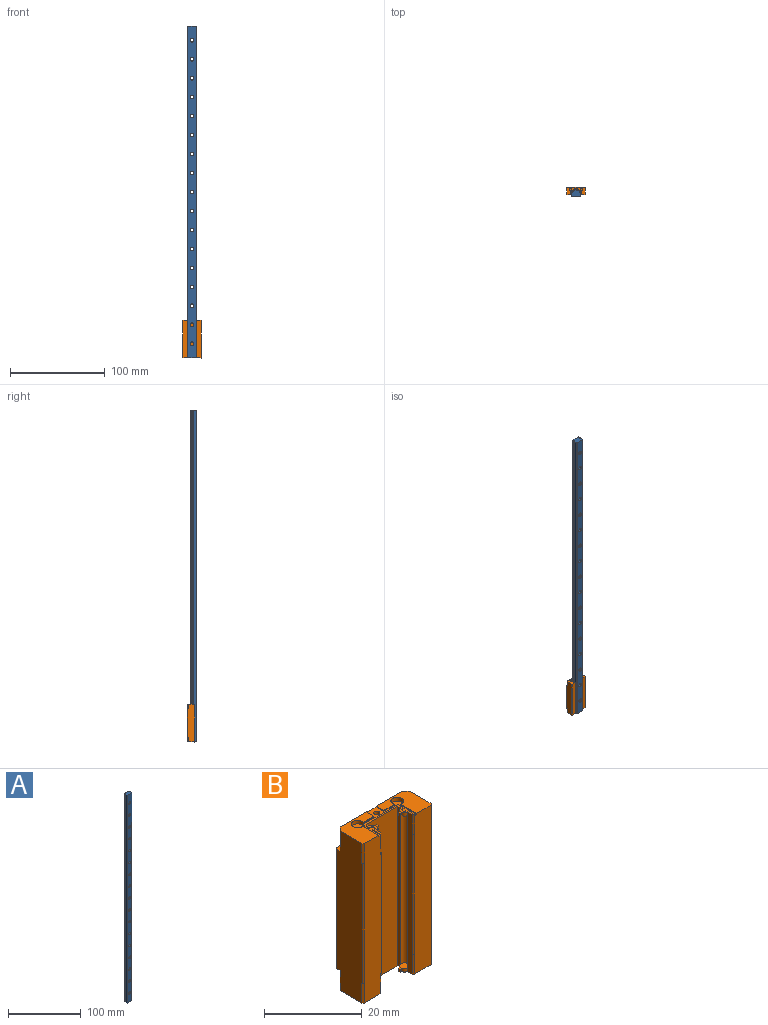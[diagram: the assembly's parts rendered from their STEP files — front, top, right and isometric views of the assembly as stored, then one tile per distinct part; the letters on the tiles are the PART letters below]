
ASSEMBLY  parts=2 mates=1
PART A: 107 faces, bbox 9x6.5x350 mm
  f0: cylinder r=1.75mm len=3.5mm, axis (0,1,0), area 30.8mm2, adj f36,f43
  f1: cylinder r=1.75mm len=3.5mm, axis (0,1,0), area 30.8mm2, adj f34,f41
  f2: cylinder r=1.75mm len=3.5mm, axis (0,1,0), area 30.8mm2, adj f32,f39
  f3: cylinder r=1.75mm len=3.5mm, axis (0,1,0), area 30.8mm2, adj f30,f37
  f4: cylinder r=1.75mm len=3.5mm, axis (0,1,0), area 30.8mm2, adj f26,f27
  f5: cylinder r=1mm len=350mm, axis (0,0,-1), area 403.5mm2, adj f6,f24,f57,f106
  f6: plane 350x0.5mm, normal (0,-1,0), area 175mm2, adj f5,f7,f57,f106
  f7: plane 350x0.5mm, normal (-1,0,0), area 175mm2, adj f6,f8,f57,f106
  f8: plane 350x0.47mm, normal (0,1,0), area 163.7mm2, adj f7,f9,f57,f106
  f9: cylinder r=1mm len=350mm, axis (0,0,-1), area 448.7mm2, adj f8,f10,f57,f106
  f10: plane 350x3.51mm, normal (-1,0,0), area 1226.8mm2, adj f9,f11,f57,f106
  f11: plane 350x0.2mm, normal (-0.71,-0.71,0), area 99mm2, adj f10,f12,f57,f106
  f12: plane 350x8.6mm, normal (0,-1,0), area 2806.9mm2, adj f11,f13,f27,f37,f39,f41,f43,f57
  f13: plane 350x0.2mm, normal (0.71,-0.71,0), area 99mm2, adj f12,f14,f57,f106
  f14: plane 350x3.51mm, normal (1,0,0), area 1226.8mm2, adj f13,f15,f57,f106
  f15: cylinder r=1mm len=350mm, axis (0,0,-1), area 448.7mm2, adj f14,f16,f57,f106
  f16: plane 350x0.47mm, normal (0,1,0), area 163.7mm2, adj f15,f17,f57,f106
  f17: plane 350x0.5mm, normal (1,0,0), area 175mm2, adj f16,f18,f57,f106
  f18: plane 350x0.5mm, normal (0,-1,0), area 175mm2, adj f17,f19,f57,f106
  f19: cylinder r=1mm len=350mm, axis (0,0,-1), area 403.5mm2, adj f18,f20,f57,f106
  f20: plane 350x0.61mm, normal (1,0,0), area 211.8mm2, adj f19,f21,f57,f106
  f21: plane 350x0.2mm, normal (0.71,0.71,0), area 99mm2, adj f20,f22,f57,f106
  f22: plane 350x8.6mm, normal (0,1,0), area 2463.1mm2, adj f21,f23,f28,f38,f40,f42,f44,f57
  f23: plane 350x0.2mm, normal (-0.71,0.71,0), area 99mm2, adj f22,f24,f57,f106
  f24: plane 350x0.61mm, normal (-1,0,0), area 211.8mm2, adj f5,f23,f57,f106
  f25: cylinder r=3mm len=6mm, axis (0,1,0), area 62.2mm2, adj f26,f28
  f26: plane 6x6mm, normal (0,1,0), area 18.7mm2, adj f4,f25
  f27: cone r=1.75mm half-angle=45deg, axis (0,-1,0), area 3.3mm2, adj f4,f12
  f28: cone r=3mm half-angle=45deg, axis (0,1,0), area 5.5mm2, adj f22,f25
  f29: cylinder r=3mm len=6mm, axis (0,1,0), area 62.2mm2, adj f30,f38
  f30: plane 6x6mm, normal (0,1,0), area 18.7mm2, adj f3,f29
  f31: cylinder r=3mm len=6mm, axis (0,1,0), area 62.2mm2, adj f32,f40
  f32: plane 6x6mm, normal (0,1,0), area 18.7mm2, adj f2,f31
  f33: cylinder r=3mm len=6mm, axis (0,1,0), area 62.2mm2, adj f34,f42
  f34: plane 6x6mm, normal (0,1,0), area 18.7mm2, adj f1,f33
  f35: cylinder r=3mm len=6mm, axis (0,1,0), area 62.2mm2, adj f36,f44
  f36: plane 6x6mm, normal (0,1,0), area 18.7mm2, adj f0,f35
  f37: cone r=1.75mm half-angle=45deg, axis (0,-1,0), area 3.3mm2, adj f3,f12
  f38: cone r=3mm half-angle=45deg, axis (0,1,0), area 5.5mm2, adj f22,f29
  f39: cone r=1.75mm half-angle=45deg, axis (0,-1,0), area 3.3mm2, adj f2,f12
  f40: cone r=3mm half-angle=45deg, axis (0,1,0), area 5.5mm2, adj f22,f31
  f41: cone r=1.75mm half-angle=45deg, axis (0,-1,0), area 3.3mm2, adj f1,f12
  f42: cone r=3mm half-angle=45deg, axis (0,1,0), area 5.5mm2, adj f22,f33
  f43: cone r=1.75mm half-angle=45deg, axis (0,-1,0), area 3.3mm2, adj f0,f12
  f44: cone r=3mm half-angle=45deg, axis (0,1,0), area 5.5mm2, adj f22,f35
  f45: cylinder r=1.75mm len=3.5mm, axis (0,1,0), area 30.8mm2, adj f83,f104
  f46: cylinder r=1.75mm len=3.5mm, axis (0,1,0), area 30.8mm2, adj f81,f102
  f47: cylinder r=1.75mm len=3.5mm, axis (0,1,0), area 30.8mm2, adj f79,f100
  f48: cylinder r=1.75mm len=3.5mm, axis (0,1,0), area 30.8mm2, adj f77,f98
  f49: cylinder r=1.75mm len=3.5mm, axis (0,1,0), area 30.8mm2, adj f75,f96
  f50: cylinder r=1.75mm len=3.5mm, axis (0,1,0), area 30.8mm2, adj f73,f94
  f51: cylinder r=1.75mm len=3.5mm, axis (0,1,0), area 30.8mm2, adj f71,f92
  f52: cylinder r=1.75mm len=3.5mm, axis (0,1,0), area 30.8mm2, adj f69,f90
  f53: cylinder r=1.75mm len=3.5mm, axis (0,1,0), area 30.8mm2, adj f67,f88
  f54: cylinder r=1.75mm len=3.5mm, axis (0,1,0), area 30.8mm2, adj f65,f86
  f55: cylinder r=1.75mm len=3.5mm, axis (0,1,0), area 30.8mm2, adj f63,f84
  f56: cylinder r=1.75mm len=3.5mm, axis (0,1,0), area 30.8mm2, adj f59,f60
  f57: plane 9x6.5mm, normal (0,0,-1), area 55.2mm2, adj f5,f6,f7,f8,f9,f10,f11,f12
  f58: cylinder r=3mm len=6mm, axis (0,1,0), area 62.2mm2, adj f59,f61
  f59: plane 6x6mm, normal (0,1,0), area 18.7mm2, adj f56,f58
  f60: cone r=1.75mm half-angle=45deg, axis (0,-1,0), area 3.3mm2, adj f12,f56
  f61: cone r=3mm half-angle=45deg, axis (0,1,0), area 5.5mm2, adj f22,f58
  f62: cylinder r=3mm len=6mm, axis (0,1,0), area 62.2mm2, adj f63,f85
  f63: plane 6x6mm, normal (0,1,0), area 18.7mm2, adj f55,f62
  f64: cylinder r=3mm len=6mm, axis (0,1,0), area 62.2mm2, adj f65,f87
  f65: plane 6x6mm, normal (0,1,0), area 18.7mm2, adj f54,f64
  f66: cylinder r=3mm len=6mm, axis (0,1,0), area 62.2mm2, adj f67,f89
  f67: plane 6x6mm, normal (0,1,0), area 18.7mm2, adj f53,f66
  f68: cylinder r=3mm len=6mm, axis (0,1,0), area 62.2mm2, adj f69,f91
  f69: plane 6x6mm, normal (0,1,0), area 18.7mm2, adj f52,f68
  f70: cylinder r=3mm len=6mm, axis (0,1,0), area 62.2mm2, adj f71,f93
  f71: plane 6x6mm, normal (0,1,0), area 18.7mm2, adj f51,f70
  f72: cylinder r=3mm len=6mm, axis (0,1,0), area 62.2mm2, adj f73,f95
  f73: plane 6x6mm, normal (0,1,0), area 18.7mm2, adj f50,f72
  f74: cylinder r=3mm len=6mm, axis (0,1,0), area 62.2mm2, adj f75,f97
  f75: plane 6x6mm, normal (0,1,0), area 18.7mm2, adj f49,f74
  f76: cylinder r=3mm len=6mm, axis (0,1,0), area 62.2mm2, adj f77,f99
  f77: plane 6x6mm, normal (0,1,0), area 18.7mm2, adj f48,f76
  f78: cylinder r=3mm len=6mm, axis (0,1,0), area 62.2mm2, adj f79,f101
  f79: plane 6x6mm, normal (0,1,0), area 18.7mm2, adj f47,f78
  f80: cylinder r=3mm len=6mm, axis (0,1,0), area 62.2mm2, adj f81,f103
  f81: plane 6x6mm, normal (0,1,0), area 18.7mm2, adj f46,f80
  f82: cylinder r=3mm len=6mm, axis (0,1,0), area 62.2mm2, adj f83,f105
  f83: plane 6x6mm, normal (0,1,0), area 18.7mm2, adj f45,f82
  f84: cone r=1.75mm half-angle=45deg, axis (0,-1,0), area 3.3mm2, adj f12,f55
  f85: cone r=3mm half-angle=45deg, axis (0,1,0), area 5.5mm2, adj f22,f62
  f86: cone r=1.75mm half-angle=45deg, axis (0,-1,0), area 3.3mm2, adj f12,f54
  f87: cone r=3mm half-angle=45deg, axis (0,1,0), area 5.5mm2, adj f22,f64
  f88: cone r=1.75mm half-angle=45deg, axis (0,-1,0), area 3.3mm2, adj f12,f53
  f89: cone r=3mm half-angle=45deg, axis (0,1,0), area 5.5mm2, adj f22,f66
  f90: cone r=1.75mm half-angle=45deg, axis (0,-1,0), area 3.3mm2, adj f12,f52
  f91: cone r=3mm half-angle=45deg, axis (0,1,0), area 5.5mm2, adj f22,f68
  f92: cone r=1.75mm half-angle=45deg, axis (0,-1,0), area 3.3mm2, adj f12,f51
  f93: cone r=3mm half-angle=45deg, axis (0,1,0), area 5.5mm2, adj f22,f70
  f94: cone r=1.75mm half-angle=45deg, axis (0,-1,0), area 3.3mm2, adj f12,f50
  f95: cone r=3mm half-angle=45deg, axis (0,1,0), area 5.5mm2, adj f22,f72
  f96: cone r=1.75mm half-angle=45deg, axis (0,-1,0), area 3.3mm2, adj f12,f49
  f97: cone r=3mm half-angle=45deg, axis (0,1,0), area 5.5mm2, adj f22,f74
  f98: cone r=1.75mm half-angle=45deg, axis (0,-1,0), area 3.3mm2, adj f12,f48
  f99: cone r=3mm half-angle=45deg, axis (0,1,0), area 5.5mm2, adj f22,f76
  f100: cone r=1.75mm half-angle=45deg, axis (0,-1,0), area 3.3mm2, adj f12,f47
  f101: cone r=3mm half-angle=45deg, axis (0,1,0), area 5.5mm2, adj f22,f78
  f102: cone r=1.75mm half-angle=45deg, axis (0,-1,0), area 3.3mm2, adj f12,f46
  f103: cone r=3mm half-angle=45deg, axis (0,1,0), area 5.5mm2, adj f22,f80
  f104: cone r=1.75mm half-angle=45deg, axis (0,-1,0), area 3.3mm2, adj f12,f45
  f105: cone r=3mm half-angle=45deg, axis (0,1,0), area 5.5mm2, adj f22,f82
  f106: plane 9x6.5mm, normal (0,0,1), area 55.2mm2, adj f5,f6,f7,f8,f9,f10,f11,f12
PART B: 137 faces, bbox 20x8x39.9 mm
  f0: plane 0.4x0.4mm, normal (0,0,1), area 0mm2, adj f17,f18,f36,f114
  f1: plane 5.5x1.3mm, normal (0,0,1), area 2.1mm2, adj f18,f24,f25,f26,f37,f110
  f2: plane 5.5x1.3mm, normal (0,0,1), area 2.1mm2, adj f20,f23,f25,f27,f34,f109
  f3: plane 0.4x0.4mm, normal (0,0,1), area 0mm2, adj f19,f20,f35,f112
  f4: plane 0.4x0.4mm, normal (0,0,1), area 0mm2, adj f19,f28,f39,f111
  f5: plane 0.4x0.4mm, normal (0,0,1), area 0mm2, adj f17,f21,f38,f113
  f6: plane 0.4x0.4mm, normal (0,0,-1), area 0mm2, adj f17,f21,f38,f50
  f7: plane 0.4x0.4mm, normal (0,0,-1), area 0mm2, adj f19,f28,f39,f51
  f8: plane 0.4x0.4mm, normal (0,0,-1), area 0mm2, adj f19,f20,f35,f52
  f9: plane 5.5x1.3mm, normal (0,0,-1), area 2.1mm2, adj f20,f23,f25,f27,f34,f48
  f10: plane 5.5x1.3mm, normal (0,0,-1), area 2.1mm2, adj f18,f24,f25,f26,f37,f47
  f11: plane 3x3mm, normal (0,1,0), area 7.1mm2, adj f13
  f12: plane 3x3mm, normal (0,1,0), area 7.1mm2, adj f14
  f13: cylinder r=1.5mm len=3mm, axis (0,1,0), area 25.4mm2, adj f11,f15
  f14: cylinder r=1.5mm len=3mm, axis (0,1,0), area 25.4mm2, adj f12,f16
  f15: cone r=1.5mm half-angle=45deg, axis (0,1,0), area 4.4mm2, adj f13,f23
  f16: cone r=1.5mm half-angle=45deg, axis (0,1,0), area 4.4mm2, adj f14,f24
  f17: plane 39.9x4.9mm, normal (0,-1,0), area 193.3mm2, adj f0,f5,f6,f36,f38,f46,f49,f50
  f18: plane 39.9x7.4mm, normal (-1,0,0), area 284.3mm2, adj f0,f1,f10,f36,f37,f46,f47,f49
  f19: plane 39.9x4.9mm, normal (0,-1,0), area 193.3mm2, adj f3,f4,f7,f8,f35,f39,f51,f52
  f20: plane 39.9x7.4mm, normal (1,0,0), area 284.3mm2, adj f2,f3,f8,f9,f34,f35,f48,f52
  f21: plane 39.9x1.41mm, normal (1,0,0), area 55.1mm2, adj f5,f6,f31,f38,f50,f56,f64,f95
  f22: plane 39.9x0.81mm, normal (-1,0,0), area 32.1mm2, adj f29,f33,f56,f59,f95,f98
  f23: plane 29.9x4.9mm, normal (0,1,0), area 126.2mm2, adj f2,f9,f15,f27,f34,f44
  f24: plane 29.9x4.9mm, normal (0,1,0), area 126.2mm2, adj f1,f10,f16,f26,f37,f45
  f25: plane 39.9x18mm, normal (0,1,0), area 448mm2, adj f1,f2,f9,f10,f26,f27,f47,f48
  f26: plane 29.9x0.3mm, normal (0.71,0.71,0), area 12.7mm2, adj f1,f10,f24,f25
  f27: plane 29.9x0.3mm, normal (-0.71,0.71,0), area 12.7mm2, adj f2,f9,f23,f25
  f28: plane 39.9x1.41mm, normal (-1,0,0), area 55.1mm2, adj f4,f7,f29,f39,f51,f56,f63,f95
  f29: cylinder r=1mm len=38.1mm, axis (0,0,-1), area 127.3mm2, adj f22,f28,f53,f93
  f30: plane 39.9x0.81mm, normal (1,0,0), area 32.1mm2, adj f31,f33,f56,f68,f95,f107
  f31: cylinder r=1mm len=38.1mm, axis (0,0,-1), area 127.3mm2, adj f21,f30,f54,f92
  f32: cylinder r=0.64mm len=39.5mm, axis (0,0,-1), area 159.8mm2, adj f75,f120
  f33: plane 39.9x9mm, normal (0,-1,0), area 359.1mm2, adj f22,f30,f56,f95
  f34: plane 29.9x0.3mm, normal (0.71,0.71,0), area 12.7mm2, adj f2,f9,f20,f23
  f35: plane 29.9x0.3mm, normal (0.71,-0.71,0), area 12.7mm2, adj f3,f8,f19,f20
  f36: plane 29.9x0.3mm, normal (-0.71,-0.71,0), area 12.7mm2, adj f0,f17,f18,f46
  f37: plane 29.9x0.3mm, normal (-0.71,0.71,0), area 12.7mm2, adj f1,f10,f18,f24
  f38: plane 29.9x0.3mm, normal (0.71,-0.71,0), area 12.7mm2, adj f5,f6,f17,f21
  f39: plane 29.9x0.3mm, normal (-0.71,-0.71,0), area 12.7mm2, adj f4,f7,f19,f28
  f40: plane 3x3mm, normal (0,1,0), area 7.1mm2, adj f42
  f41: plane 3x3mm, normal (0,1,0), area 7.1mm2, adj f43
  f42: cylinder r=1.5mm len=3mm, axis (0,1,0), area 25.4mm2, adj f40,f44
  f43: cylinder r=1.5mm len=3mm, axis (0,1,0), area 25.4mm2, adj f41,f45
  f44: cone r=1.5mm half-angle=45deg, axis (0,1,0), area 4.4mm2, adj f23,f42
  f45: cone r=1.5mm half-angle=45deg, axis (0,1,0), area 4.4mm2, adj f24,f43
  f46: plane 0.4x0.4mm, normal (0,0,-1), area 0mm2, adj f17,f18,f36,f49
  f47: plane 5x1mm, normal (-0.71,0.71,0), area 7.1mm2, adj f10,f18,f25,f58
  f48: plane 5x1mm, normal (0.71,0.71,0), area 7.1mm2, adj f9,f20,f25,f55
  f49: plane 5x0.4mm, normal (-0.71,-0.71,0), area 2.8mm2, adj f17,f18,f46,f58
  f50: plane 5x0.4mm, normal (0.71,-0.71,0), area 2.8mm2, adj f6,f17,f21,f56
  f51: plane 5x0.4mm, normal (-0.71,-0.71,0), area 2.8mm2, adj f7,f19,f28,f56
  f52: plane 5x0.4mm, normal (0.71,-0.71,0), area 2.8mm2, adj f8,f19,f20,f55
  f53: plane 2.47x2mm, normal (0,0,1), area 3.4mm2, adj f29,f59,f60,f61,f62,f63
  f54: plane 2.47x2mm, normal (0,0,1), area 3.4mm2, adj f31,f64,f65,f66,f67,f68
  f55: plane 8.58x7.7mm, normal (0,0,-1), area 38.3mm2, adj f19,f20,f25,f48,f52,f69,f71,f72
  f56: plane 10x5mm, normal (0,0,-1), area 10.9mm2, adj f17,f19,f21,f22,f28,f30,f33,f50
  f57: cylinder r=1.3mm len=2.6mm, axis (0,0,1), area 7.1mm2, adj f56,f58,f73,f74,f75,f78,f79,f82
  f58: plane 8.58x7.7mm, normal (0,0,-1), area 38.3mm2, adj f17,f18,f25,f47,f49,f57,f70,f74
  f59: cylinder r=1mm len=0.9mm, axis (0,0,1), area 1.1mm2, adj f22,f53,f56,f60
  f60: plane 0.9x0.5mm, normal (0,1,0), area 0.4mm2, adj f53,f56,f59,f61
  f61: plane 0.9x0.5mm, normal (-1,0,0), area 0.4mm2, adj f53,f56,f60,f62
  f62: plane 0.9x0.5mm, normal (0,-1,0), area 0.4mm2, adj f53,f56,f61,f63
  f63: cylinder r=1mm len=0.9mm, axis (0,0,1), area 1.1mm2, adj f28,f53,f56,f62
  f64: cylinder r=1mm len=0.9mm, axis (0,0,1), area 1.1mm2, adj f21,f54,f56,f65
  f65: plane 0.9x0.5mm, normal (0,-1,0), area 0.4mm2, adj f54,f56,f64,f66
  f66: plane 0.9x0.5mm, normal (1,0,0), area 0.4mm2, adj f54,f56,f65,f67
  f67: plane 0.9x0.5mm, normal (0,1,0), area 0.4mm2, adj f54,f56,f66,f68
  f68: cylinder r=1mm len=0.9mm, axis (0,0,1), area 1.1mm2, adj f30,f54,f56,f67
  f69: cylinder r=1.3mm len=2.6mm, axis (0,0,1), area 7.1mm2, adj f55,f56,f72,f73,f75,f85,f86,f89
  f70: plane 2.2x0.2mm, normal (1,0,0), area 0.4mm2, adj f25,f58,f74,f75
  f71: plane 2.2x0.2mm, normal (-1,0,0), area 0.4mm2, adj f25,f55,f72,f75
  f72: plane 3.09x0.2mm, normal (0,-1,0), area 0.6mm2, adj f55,f69,f71,f75
  f73: plane 9.63x0.2mm, normal (0,1,0), area 1.9mm2, adj f56,f57,f69,f75
  f74: plane 3.09x0.2mm, normal (0,-1,0), area 0.6mm2, adj f57,f58,f70,f75
  f75: plane 9.63x2.7mm, normal (0,0,-1), area 9.6mm2, adj f25,f32,f57,f69,f70,f71,f72,f73
  f76: plane 0.45x0.2mm, normal (0,1,0), area 0.1mm2, adj f56,f77,f81,f82
  f77: plane 2.2x0.2mm, normal (-1,0,0), area 0.4mm2, adj f17,f56,f76,f82
  f78: plane 4.64x0.2mm, normal (1,0,0), area 0.9mm2, adj f17,f57,f58,f82
  f79: plane 1.65x0.2mm, normal (-1,0,0), area 0.3mm2, adj f56,f57,f80,f82
  f80: plane 0.4x0.2mm, normal (0,-1,0), area 0.1mm2, adj f56,f79,f81,f82
  f81: cylinder r=0.5mm len=1mm, axis (0,0,-1), area 0.3mm2, adj f56,f76,f80,f82
  f82: plane 4.85x1.4mm, normal (0,0,-1), area 3.2mm2, adj f17,f57,f76,f77,f78,f79,f80,f81
  f83: cylinder r=0.5mm len=1mm, axis (0,0,-1), area 0.3mm2, adj f56,f84,f88,f89
  f84: plane 0.4x0.2mm, normal (0,-1,0), area 0.1mm2, adj f56,f83,f85,f89
  f85: plane 1.65x0.2mm, normal (1,0,0), area 0.3mm2, adj f56,f69,f84,f89
  f86: plane 4.64x0.2mm, normal (-1,0,0), area 0.9mm2, adj f19,f55,f69,f89
  f87: plane 2.2x0.2mm, normal (1,0,0), area 0.4mm2, adj f19,f56,f88,f89
  f88: plane 0.45x0.2mm, normal (0,1,0), area 0.1mm2, adj f56,f83,f87,f89
  f89: plane 4.85x1.4mm, normal (0,0,-1), area 3.2mm2, adj f19,f69,f83,f84,f85,f86,f87,f88
  f90: plane 2.6x2.6mm, normal (0,0,-1), area 5.3mm2, adj f57
  f91: plane 2.6x2.6mm, normal (0,0,-1), area 5.3mm2, adj f69
  f92: plane 2.47x2mm, normal (0,0,-1), area 3.4mm2, adj f31,f103,f104,f105,f106,f107
  f93: plane 2.47x2mm, normal (0,0,-1), area 3.4mm2, adj f29,f98,f99,f100,f101,f102
  f94: plane 8.58x7.7mm, normal (0,0,1), area 38.3mm2, adj f19,f20,f25,f108,f109,f112,f116,f117
  f95: plane 10x5mm, normal (0,0,1), area 10.9mm2, adj f17,f19,f21,f22,f28,f30,f33,f96
  f96: cylinder r=1.3mm len=2.6mm, axis (0,0,-1), area 7.1mm2, adj f95,f97,f118,f119,f120,f123,f124,f127
  f97: plane 8.58x7.7mm, normal (0,0,1), area 38.3mm2, adj f17,f18,f25,f96,f110,f114,f115,f119
  f98: cylinder r=1mm len=0.9mm, axis (0,0,-1), area 1.1mm2, adj f22,f93,f95,f99
  f99: plane 0.9x0.5mm, normal (0,1,0), area 0.4mm2, adj f93,f95,f98,f100
  f100: plane 0.9x0.5mm, normal (-1,0,0), area 0.4mm2, adj f93,f95,f99,f101
  f101: plane 0.9x0.5mm, normal (0,-1,0), area 0.4mm2, adj f93,f95,f100,f102
  f102: cylinder r=1mm len=0.9mm, axis (0,0,-1), area 1.1mm2, adj f28,f93,f95,f101
  f103: cylinder r=1mm len=0.9mm, axis (0,0,-1), area 1.1mm2, adj f21,f92,f95,f104
  f104: plane 0.9x0.5mm, normal (0,-1,0), area 0.4mm2, adj f92,f95,f103,f105
  f105: plane 0.9x0.5mm, normal (1,0,0), area 0.4mm2, adj f92,f95,f104,f106
  f106: plane 0.9x0.5mm, normal (0,1,0), area 0.4mm2, adj f92,f95,f105,f107
  f107: cylinder r=1mm len=0.9mm, axis (0,0,-1), area 1.1mm2, adj f30,f92,f95,f106
  f108: cylinder r=1.3mm len=2.6mm, axis (0,0,-1), area 7.1mm2, adj f94,f95,f117,f118,f120,f130,f131,f134
  f109: plane 5x1mm, normal (0.71,0.71,0), area 7.1mm2, adj f2,f20,f25,f94
  f110: plane 5x1mm, normal (-0.71,0.71,0), area 7.1mm2, adj f1,f18,f25,f97
  f111: plane 5x0.4mm, normal (-0.71,-0.71,0), area 2.8mm2, adj f4,f19,f28,f95
  f112: plane 5x0.4mm, normal (0.71,-0.71,0), area 2.8mm2, adj f3,f19,f20,f94
  f113: plane 5x0.4mm, normal (0.71,-0.71,0), area 2.8mm2, adj f5,f17,f21,f95
  f114: plane 5x0.4mm, normal (-0.71,-0.71,0), area 2.8mm2, adj f0,f17,f18,f97
  f115: plane 2.2x0.2mm, normal (1,0,0), area 0.4mm2, adj f25,f97,f119,f120
  f116: plane 2.2x0.2mm, normal (-1,0,0), area 0.4mm2, adj f25,f94,f117,f120
  f117: plane 3.09x0.2mm, normal (0,-1,0), area 0.6mm2, adj f94,f108,f116,f120
  f118: plane 9.63x0.2mm, normal (0,1,0), area 1.9mm2, adj f95,f96,f108,f120
  f119: plane 3.09x0.2mm, normal (0,-1,0), area 0.6mm2, adj f96,f97,f115,f120
  f120: plane 9.63x2.7mm, normal (0,0,1), area 9.6mm2, adj f25,f32,f96,f108,f115,f116,f117,f118
  f121: plane 0.45x0.2mm, normal (0,1,0), area 0.1mm2, adj f95,f122,f126,f127
  f122: plane 2.2x0.2mm, normal (-1,0,0), area 0.4mm2, adj f17,f95,f121,f127
  f123: plane 4.64x0.2mm, normal (1,0,0), area 0.9mm2, adj f17,f96,f97,f127
  f124: plane 1.65x0.2mm, normal (-1,0,0), area 0.3mm2, adj f95,f96,f125,f127
  f125: plane 0.4x0.2mm, normal (0,-1,0), area 0.1mm2, adj f95,f124,f126,f127
  f126: cylinder r=0.5mm len=1mm, axis (0,0,1), area 0.3mm2, adj f95,f121,f125,f127
  f127: plane 4.85x1.4mm, normal (0,0,1), area 3.2mm2, adj f17,f96,f121,f122,f123,f124,f125,f126
  f128: cylinder r=0.5mm len=1mm, axis (0,0,1), area 0.3mm2, adj f95,f129,f133,f134
  f129: plane 0.4x0.2mm, normal (0,-1,0), area 0.1mm2, adj f95,f128,f130,f134
  f130: plane 1.65x0.2mm, normal (1,0,0), area 0.3mm2, adj f95,f108,f129,f134
  f131: plane 4.64x0.2mm, normal (-1,0,0), area 0.9mm2, adj f19,f94,f108,f134
  f132: plane 2.2x0.2mm, normal (1,0,0), area 0.4mm2, adj f19,f95,f133,f134
  f133: plane 0.45x0.2mm, normal (0,1,0), area 0.1mm2, adj f95,f128,f132,f134
  f134: plane 4.85x1.4mm, normal (0,0,1), area 3.2mm2, adj f19,f108,f128,f129,f130,f131,f132,f133
  f135: plane 2.6x2.6mm, normal (0,0,1), area 5.3mm2, adj f108
  f136: plane 2.6x2.6mm, normal (0,0,1), area 5.3mm2, adj f96
PLACE A t=(-27.37,-0.93,9.7)mm
PLACE B t=(-27.39,1.88,29.65)mm
MATE slider B.f56 <-> A.f57  axis (0,0,1) through (-30.52,0.33,9.7)mm
